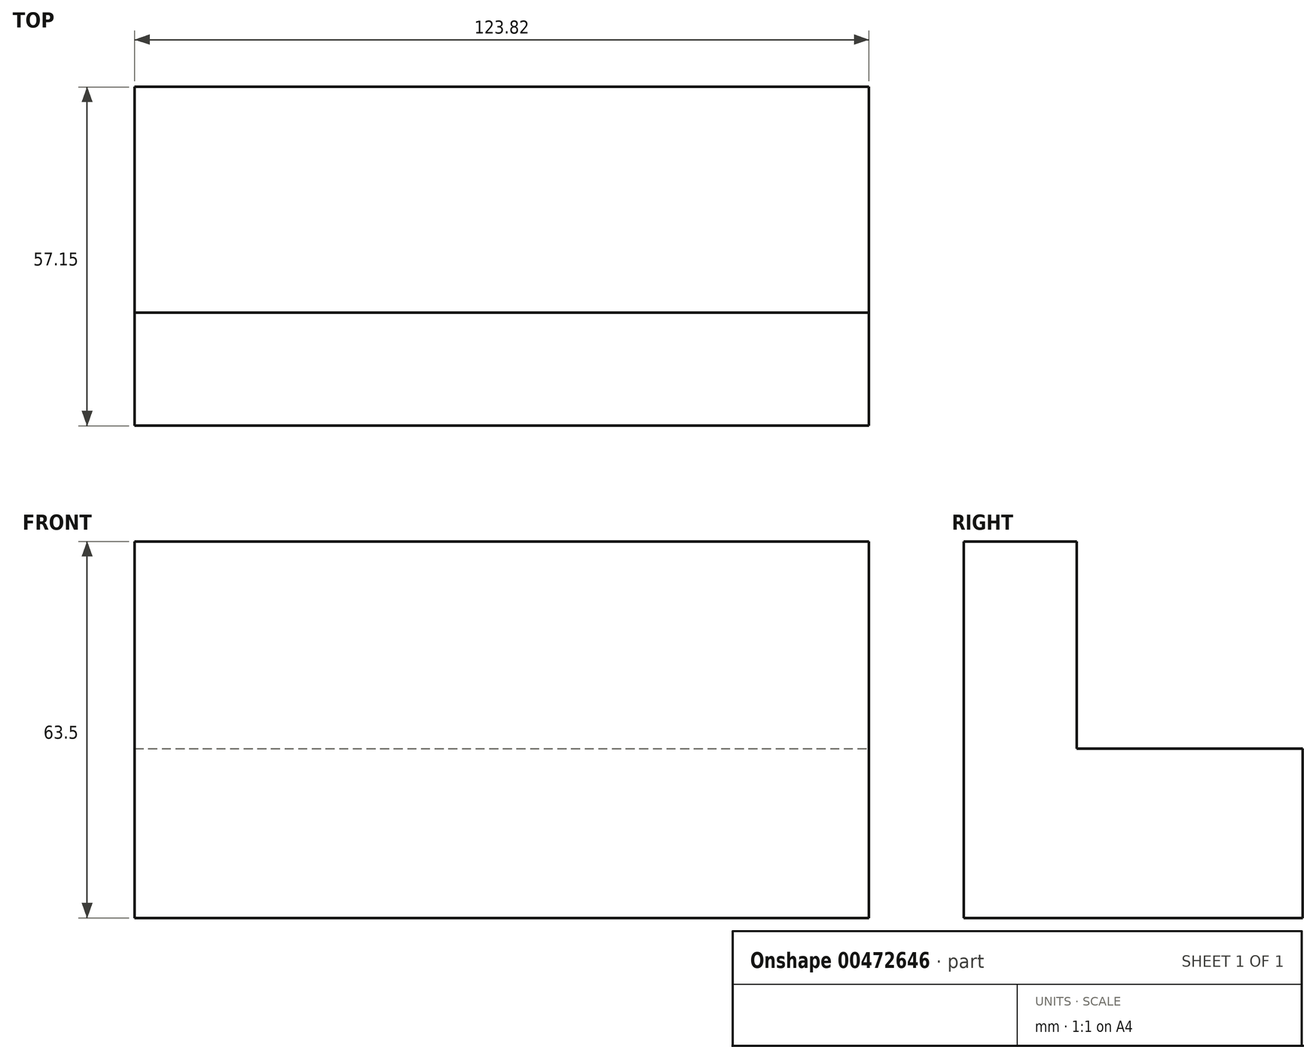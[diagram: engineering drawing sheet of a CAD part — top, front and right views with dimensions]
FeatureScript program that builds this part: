
annotation { "Feature Type Name" : "Feature", "Feature Type Description" : "" }
export const myFeature = defineFeature(function(context is Context, id is Id, definition is map)
    precondition{}
    {
        {
            var Q0;
            Q0=qCreatedBy(makeId("Top.planeOp"),FACE);
            var sketch = newSketch(context, id + "F0", { "sketchPlane" : qUnion([Q0])});
            skLineSegment(sketch, "E0.bottom", {"start": v(-61, 14.57) * mm, "end": v(62.83, 14.57) * mm});
            skLineSegment(sketch, "E0.top", {"start": v(-61, -42.58) * mm, "end": v(62.83, -42.58) * mm});
            skLineSegment(sketch, "E0.left", {"start": v(-61, 14.57) * mm, "end": v(-61, -42.58) * mm});
            skLineSegment(sketch, "E0.right", {"start": v(62.83, 14.57) * mm, "end": v(62.83, -42.58) * mm});
            skSolve(sketch);
        }
        {
            var Q0;
            Q0 = qSketchRegion(id + "F0", true);
            extrude(context, id + "F1", {"entities" : qUnion([Q0]), "depth" : 63.5 * mm});
        }
        {
            var Q0;
            Q0=makeQuery(id+"F1.opExtrude","SWEPT_FACE",FACE,{"disambiguationData":[OSD([sQuery(id+"F0.wireOp",EDGE,"E0.right")])]});
            var sketch = newSketch(context, id + "F2", { "sketchPlane" : qUnion([Q0])});
            skLineSegment(sketch, "E1.bottom", {"start": v(14.57, 63.5) * mm, "end": v(-23.53, 63.5) * mm});
            skLineSegment(sketch, "E1.top", {"start": v(14.57, 28.58) * mm, "end": v(-23.53, 28.57) * mm});
            skLineSegment(sketch, "E1.left", {"start": v(14.57, 63.5) * mm, "end": v(14.57, 28.58) * mm});
            skLineSegment(sketch, "E1.right", {"start": v(-23.53, 63.5) * mm, "end": v(-23.53, 28.57) * mm});
            skSolve(sketch);
        }
        {
            var Q0;
            Q0=makeQuery(id+"F2.imprint","IMPRINT",FACE,{"disambiguationData":[TD([[makeQuery(id+"F2.imprint","IMPRINT",EDGE,{"derivedFrom":sQuery(id+"F2.wireOp",EDGE,"E1.bottom")}),1.0]])]});
            extrude(context, id + "F3", {"entities" : qUnion([Q0]), "operationType" : NewBodyOperationType.REMOVE, "oppositeDirection" : true, "depth" : 123.82 * mm});
        }
    });
